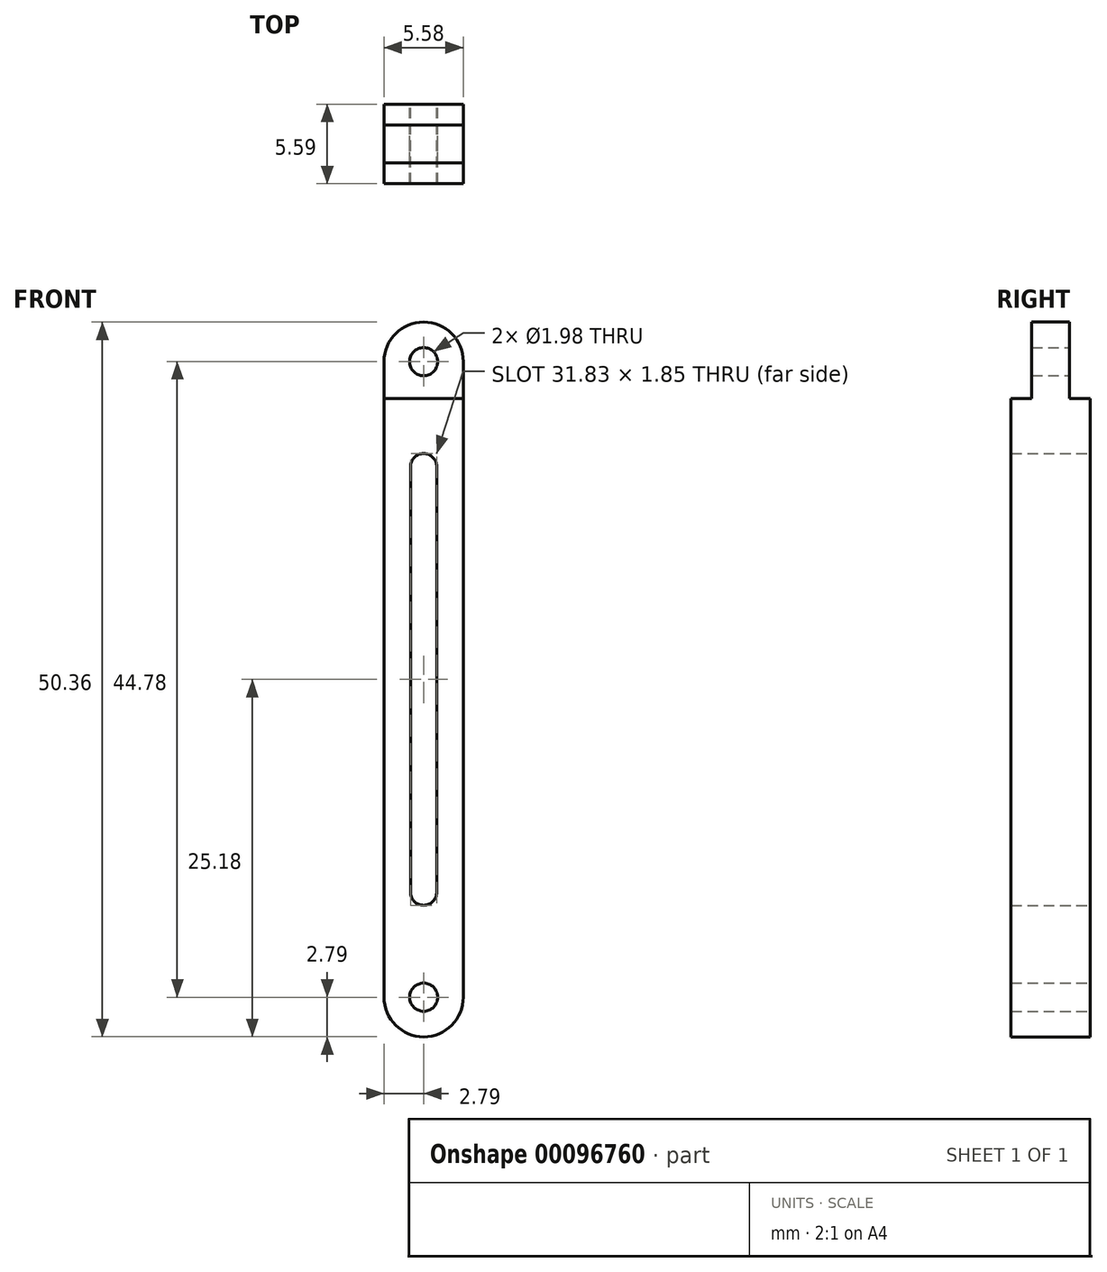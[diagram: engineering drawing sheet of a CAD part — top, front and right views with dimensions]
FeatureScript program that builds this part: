
annotation { "Feature Type Name" : "Feature", "Feature Type Description" : "" }
export const myFeature = defineFeature(function(context is Context, id is Id, definition is map)
    precondition{}
    {
        {
            var Q0;
            Q0=qCreatedBy(makeId("Front.planeOp"),FACE);
            var sketch = newSketch(context, id + "F0", { "sketchPlane" : qUnion([Q0])});
            skLineSegment(sketch, "E0.bottom", {"start": v(2.8, 16.8) * mm, "end": v(-2.8, 16.8) * mm});
            skLineSegment(sketch, "E0.top", {"start": v(2.8, -16.8) * mm, "end": v(-2.8, -16.8) * mm});
            skLineSegment(sketch, "E0.left", {"start": v(2.8, 16.8) * mm, "end": v(2.8, -16.8) * mm});
            skLineSegment(sketch, "E0.right", {"start": v(-2.8, 16.8) * mm, "end": v(-2.8, -16.8) * mm});
            skPoint(sketch, "E0.middle", {"position": v(0, 0) * mm});
            skLineSegment(sketch, "E1.bottom", {"start": v(0.93, 14.99) * mm, "end": v(-0.93, 14.99) * mm});
            skLineSegment(sketch, "E1.top", {"start": v(0.93, -14.99) * mm, "end": v(-0.93, -14.99) * mm});
            skLineSegment(sketch, "E1.left", {"start": v(0.93, 14.99) * mm, "end": v(0.93, -14.99) * mm});
            skLineSegment(sketch, "E1.right", {"start": v(-0.93, 14.99) * mm, "end": v(-0.93, -14.99) * mm});
            skArc(sketch, "E2", {"start": v(0.93, 14.99) * mm, "mid": v(0, 15.91) * mm, "end": v(-0.93, 14.99) * mm});
            skArc(sketch, "E3", {"start": v(-0.93, -14.99) * mm, "mid": v(0, -15.91) * mm, "end": v(0.93, -14.99) * mm});
            skLineSegment(sketch, "E4", {"start": v(-2.8, 16.8) * mm, "end": v(-2.8, 22.4) * mm});
            skLineSegment(sketch, "E5", {"start": v(2.8, 16.8) * mm, "end": v(2.8, 22.4) * mm});
            skArc(sketch, "E6", {"start": v(2.8, 22.4) * mm, "mid": v(0, 25.18) * mm, "end": v(-2.8, 22.4) * mm});
            skLineSegment(sketch, "E7", {"start": v(-2.8, -16.8) * mm, "end": v(-2.8, -22.4) * mm});
            skLineSegment(sketch, "E8", {"start": v(2.8, -16.8) * mm, "end": v(2.8, -22.4) * mm});
            skArc(sketch, "E9", {"start": v(-2.8, -22.4) * mm, "mid": v(0, -25.18) * mm, "end": v(2.8, -22.4) * mm});
            skCircle(sketch, "E10", {"center": v(0, -22.4) * mm, "radius": 1 * mm});
            skCircle(sketch, "E11", {"center": v(0, 22.4) * mm, "radius": 1 * mm});
            skSolve(sketch);
        }
        {
            var Q0;
            Q0=sQuery(id+"F0.wireOp",EDGE,"E1.left");
            var Q1;
            Q1=sQuery(id+"F0.wireOp",EDGE,"E1.right");
            var Q2;
            Q2=sQuery(id+"F0.wireOp",EDGE,"E2");
            var Q3;
            Q3=sQuery(id+"F0.wireOp",EDGE,"E3");
            extrude(context, id + "F1", {"bodyType" : ToolBodyType.SURFACE, "surfaceEntities" : qUnion([Q0, Q1, Q2, Q3]), "depth" : 5.6 * mm});
        }
        {
            var Q0;
            Q0 = qSketchRegion(id + "F0", true);
            extrude(context, id + "F2", {"entities" : qUnion([Q0]), "depth" : 5.6 * mm});
        }
        {
            var Q0;
            Q0=makeQuery(id+"F2.opExtrude","SWEPT_FACE",FACE,{"disambiguationData":[OSD([sQuery(id+"F0.wireOp",EDGE,"E0.right"),sQuery(id+"F0.wireOp",EDGE,"E4"),sQuery(id+"F0.wireOp",EDGE,"E7")])]});
            var sketch = newSketch(context, id + "F3", { "sketchPlane" : qUnion([Q0])});
            skLineSegment(sketch, "E12", {"start": v(0, 19.8) * mm, "end": v(1.46, 19.8) * mm});
            skLineSegment(sketch, "E13", {"start": v(1.46, 19.8) * mm, "end": v(1.46, 25.18) * mm});
            skLineSegment(sketch, "E14", {"start": v(4.13, 25.18) * mm, "end": v(4.13, 19.8) * mm});
            skLineSegment(sketch, "E15", {"start": v(4.13, 19.8) * mm, "end": v(5.59, 19.8) * mm});
            skLineSegment(sketch, "E16", {"start": v(2.8, 0) * mm, "end": v(2.8, 34.17) * mm, "construction": true});
            skPoint(sketch, "E16.startSnap0", {"position": v(2.8, 22.4) * mm});
            skLineSegment(sketch, "E17.0.0", {"start": v(0, 25.18) * mm, "end": v(0, 22.4) * mm});
            skLineSegment(sketch, "E17.0.2", {"start": v(5.59, 22.4) * mm, "end": v(5.59, 25.18) * mm});
            skLineSegment(sketch, "E18.MirrorCS", {"start": v(0, -19.8) * mm, "end": v(1.46, -19.8) * mm});
            skPoint(sketch, "E19.MirrorP", {"position": v(2.8, -22.4) * mm});
            skLineSegment(sketch, "E20.MirrorCS", {"start": v(4.13, -25.18) * mm, "end": v(4.13, -19.8) * mm});
            skLineSegment(sketch, "E21.MirrorCS", {"start": v(5.59, -22.4) * mm, "end": v(5.59, -25.18) * mm});
            skLineSegment(sketch, "E22.MirrorCS", {"start": v(1.46, -19.8) * mm, "end": v(1.46, -25.18) * mm});
            skLineSegment(sketch, "E23.MirrorCS", {"start": v(0, -25.18) * mm, "end": v(0, -22.4) * mm});
            skLineSegment(sketch, "E24.MirrorCS", {"start": v(4.13, -19.8) * mm, "end": v(5.59, -19.8) * mm});
            skLineSegment(sketch, "E25", {"start": v(1.46, 25.18) * mm, "end": v(0, 25.18) * mm});
            skLineSegment(sketch, "E26", {"start": v(4.13, 25.18) * mm, "end": v(5.59, 25.18) * mm});
            skLineSegment(sketch, "E27", {"start": v(4.13, -25.18) * mm, "end": v(5.59, -25.18) * mm});
            skLineSegment(sketch, "E28", {"start": v(1.46, -25.18) * mm, "end": v(0, -25.18) * mm});
            skLineSegment(sketch, "E29.0.1", {"start": v(1.46, 22.4) * mm, "end": v(4.13, 22.4) * mm});
            skLineSegment(sketch, "E29.0.3", {"start": v(4.13, 22.4) * mm, "end": v(1.46, 22.4) * mm});
            skLineSegment(sketch, "E30", {"start": v(0, 25.18) * mm, "end": v(5.59, 25.18) * mm, "construction": true});
            skPoint(sketch, "E31.orphan", {"position": v(0, 22.4) * mm});
            skPoint(sketch, "E32.orphan", {"position": v(5.59, 22.4) * mm});
            skLineSegment(sketch, "E33", {"start": v(0, 22.4) * mm, "end": v(0, 19.8) * mm});
            skLineSegment(sketch, "E34", {"start": v(5.59, 19.8) * mm, "end": v(5.59, 22.4) * mm});
            skSolve(sketch);
        }
        {
            var Q0;
            {var subQ0=sQuery(id+"F3.wireOp",EDGE,"E12");Q0=makeQuery(id+"F3.imprint","IMPRINT",FACE,{"disambiguationData":[TD([[makeQuery(id+"F3.imprint","IMPRINT",EDGE,{"derivedFrom":subQ0}),1.0]])]});}
            var Q1;
            {var subQ0=sQuery(id+"F3.wireOp",EDGE,"E25");Q1=makeQuery(id+"F3.imprint","IMPRINT",FACE,{"disambiguationData":[TD([[makeQuery(id+"F3.imprint","IMPRINT",EDGE,{"derivedFrom":subQ0}),1.0]])]});}
            var Q2;
            {var subQ0=sQuery(id+"F3.wireOp",EDGE,"E26");Q2=makeQuery(id+"F3.imprint","IMPRINT",FACE,{"disambiguationData":[TD([[makeQuery(id+"F3.imprint","IMPRINT",EDGE,{"derivedFrom":subQ0}),-1.0]])]});}
            var Q3;
            {var subQ0=sQuery(id+"F3.wireOp",EDGE,"E15");Q3=makeQuery(id+"F3.imprint","IMPRINT",FACE,{"disambiguationData":[TD([[makeQuery(id+"F3.imprint","IMPRINT",EDGE,{"derivedFrom":subQ0}),1.0]])]});}
            extrude(context, id + "F4", {"entities" : qUnion([Q0, Q1, Q2, Q3]), "operationType" : NewBodyOperationType.REMOVE, "endBound" : BoundingType.THROUGH_ALL, "oppositeDirection" : true, "depth" : 25.4 * mm});
        }
    });
